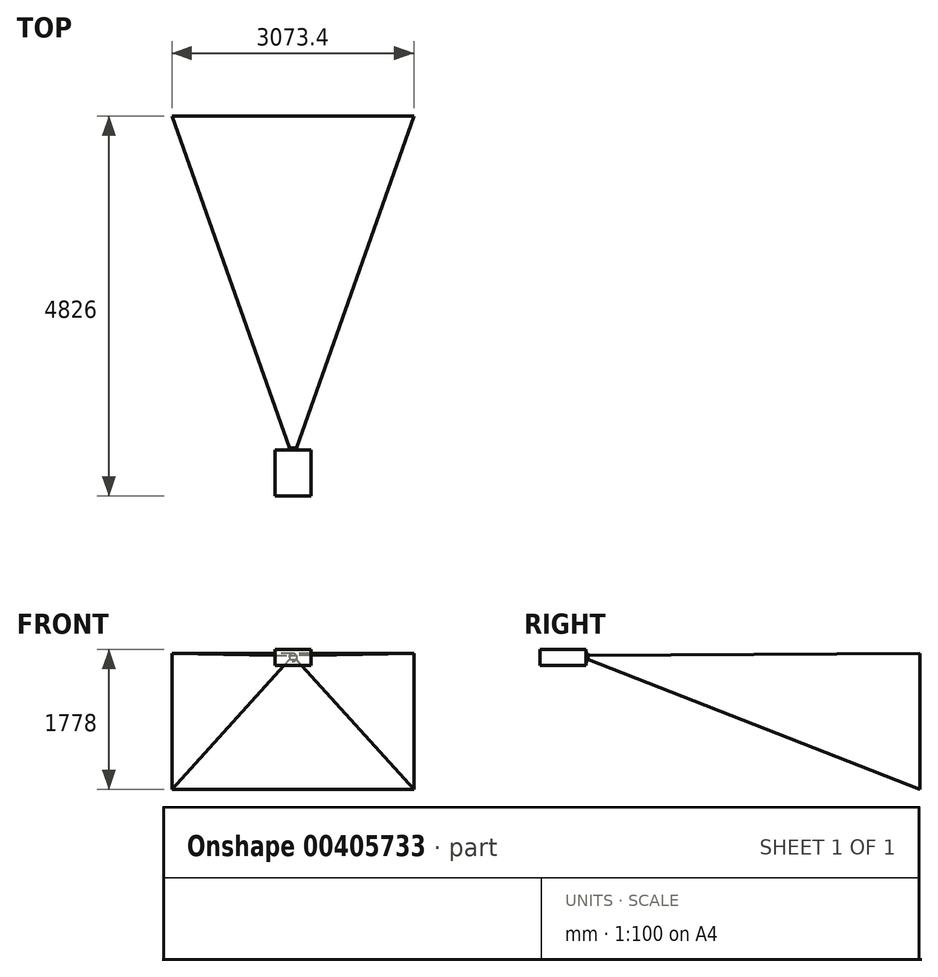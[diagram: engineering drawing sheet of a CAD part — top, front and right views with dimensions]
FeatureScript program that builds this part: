
annotation { "Feature Type Name" : "Feature", "Feature Type Description" : "" }
export const myFeature = defineFeature(function(context is Context, id is Id, definition is map)
    precondition{}
    {
        {
            var Q0;
            Q0=qCreatedBy(makeId("Front.planeOp"),FACE);
            var sketch = newSketch(context, id + "F0", { "sketchPlane" : qUnion([Q0])});
            skLineSegment(sketch, "E0.bottom", {"start": v(1536.7, 863.6) * mm, "end": v(-1536.7, 863.6) * mm});
            skLineSegment(sketch, "E0.top", {"start": v(1536.7, -863.6) * mm, "end": v(-1536.7, -863.6) * mm});
            skLineSegment(sketch, "E0.left", {"start": v(1536.7, 863.6) * mm, "end": v(1536.7, -863.6) * mm});
            skLineSegment(sketch, "E0.right", {"start": v(-1536.7, 863.6) * mm, "end": v(-1536.7, -863.6) * mm});
            skPoint(sketch, "E0.middle", {"position": v(0, 0) * mm});
            skSolve(sketch);
        }
        {
            var Q0;
            Q0=qCreatedBy(makeId("Front.planeOp"),FACE);
            cPlane(context, id + "F1", {"entities" : qUnion([Q0]), "cplaneType" : CPlaneType.OFFSET, "offset" : 4216.4 * mm, "width" : 152.4 * mm, "height" : 152.4 * mm});
        }
        {
            var Q0;
            Q0=qCreatedBy(id+"F1.planeOp",FACE);
            var sketch = newSketch(context, id + "F2", { "sketchPlane" : qUnion([Q0])});
            skCircle(sketch, "E1", {"center": v(0, 812.8) * mm, "radius": 50.8 * mm});
            skLineSegment(sketch, "E2.0", {"start": v(1536.7, 863.6) * mm, "end": v(-1536.7, 863.6) * mm, "construction": true});
            skLineSegment(sketch, "E3.bottom", {"start": v(-228.6, 914.4) * mm, "end": v(228.6, 914.4) * mm});
            skLineSegment(sketch, "E3.top", {"start": v(-228.6, 711.2) * mm, "end": v(228.6, 711.2) * mm});
            skLineSegment(sketch, "E3.left", {"start": v(-228.6, 914.4) * mm, "end": v(-228.6, 711.2) * mm});
            skLineSegment(sketch, "E3.right", {"start": v(228.6, 914.4) * mm, "end": v(228.6, 711.2) * mm});
            skLineSegment(sketch, "E4", {"start": v(-228.6, 914.4) * mm, "end": v(228.6, 711.2) * mm, "construction": true});
            skLineSegment(sketch, "E5.bottom", {"start": v(-44, 838.2) * mm, "end": v(44, 838.2) * mm});
            skLineSegment(sketch, "E5.top", {"start": v(-44, 787.4) * mm, "end": v(44, 787.4) * mm});
            skLineSegment(sketch, "E5.left", {"start": v(-44, 838.2) * mm, "end": v(-44, 787.4) * mm});
            skLineSegment(sketch, "E5.right", {"start": v(44, 838.2) * mm, "end": v(44, 787.4) * mm});
            skSolve(sketch);
        }
        {
            var Q0;
            Q0=makeQuery(id+"F0.imprint","IMPRINT",FACE,{"disambiguationData":[TD([[makeQuery(id+"F0.imprint","IMPRINT",EDGE,{"derivedFrom":sQuery(id+"F0.wireOp",EDGE,"E0.bottom")}),1.0]])]});
            var Q1;
            Q1=makeQuery(id+"F2.imprint","IMPRINT",FACE,{"disambiguationData":[TD([[makeQuery(id+"F2.imprint","IMPRINT",EDGE,{"derivedFrom":sQuery(id+"F2.wireOp",EDGE,"E5.bottom")}),-1.0]])]});
            loft(context, id + "F3", {"sheetProfilesArray" : [{ "sheetProfileEntities" : qUnion([Q0]) }, { "sheetProfileEntities" : qUnion([Q1]) }]});
        }
        {
            var Q0;
            {var subQ0=sQuery(id+"F2.wireOp",EDGE,"E5.bottom");Q0=makeQuery(id+"F2.imprint","IMPRINT",FACE,{"disambiguationData":[TD([[makeQuery(id+"F2.imprint","IMPRINT",EDGE,{"derivedFrom":subQ0}),1.0]])]});}
            var Q1;
            Q1=makeQuery(id+"F2.imprint","IMPRINT",FACE,{"disambiguationData":[TD([[makeQuery(id+"F2.imprint","IMPRINT",EDGE,{"derivedFrom":sQuery(id+"F2.wireOp",EDGE,"E5.bottom")}),-1.0]])]});
            var Q2;
            {var subQ0=sQuery(id+"F2.wireOp",EDGE,"E5.top");Q2=makeQuery(id+"F2.imprint","IMPRINT",FACE,{"disambiguationData":[TD([[makeQuery(id+"F2.imprint","IMPRINT",EDGE,{"derivedFrom":subQ0}),-1.0]])]});}
            var Q3;
            {var subQ0=sQuery(id+"F2.wireOp",EDGE,"E5.left");Q3=makeQuery(id+"F2.imprint","IMPRINT",FACE,{"disambiguationData":[TD([[makeQuery(id+"F2.imprint","IMPRINT",EDGE,{"derivedFrom":subQ0}),-1.0]])]});}
            var Q4;
            {var subQ0=sQuery(id+"F2.wireOp",EDGE,"E5.right");Q4=makeQuery(id+"F2.imprint","IMPRINT",FACE,{"disambiguationData":[TD([[makeQuery(id+"F2.imprint","IMPRINT",EDGE,{"derivedFrom":subQ0}),1.0]])]});}
            extrude(context, id + "F4", {"entities" : qUnion([Q0, Q1, Q2, Q3, Q4]), "depth" : 25.4 * mm, "offsetDistance" : 25.4 * mm});
        }
        {
            var Q0;
            {var subQ0=sQuery(id+"F2.wireOp",EDGE,"E5.right");Q0=makeQuery(id+"F2.imprint","IMPRINT",FACE,{"disambiguationData":[TD([[makeQuery(id+"F2.imprint","IMPRINT",EDGE,{"derivedFrom":subQ0}),1.0]])]});}
            var Q1;
            {var subQ0=sQuery(id+"F2.wireOp",EDGE,"E5.bottom");Q1=makeQuery(id+"F2.imprint","IMPRINT",FACE,{"disambiguationData":[TD([[makeQuery(id+"F2.imprint","IMPRINT",EDGE,{"derivedFrom":subQ0}),1.0]])]});}
            var Q2;
            {var subQ0=sQuery(id+"F2.wireOp",EDGE,"E5.top");Q2=makeQuery(id+"F2.imprint","IMPRINT",FACE,{"disambiguationData":[TD([[makeQuery(id+"F2.imprint","IMPRINT",EDGE,{"derivedFrom":subQ0}),-1.0]])]});}
            var Q3;
            {var subQ0=sQuery(id+"F2.wireOp",EDGE,"E5.left");Q3=makeQuery(id+"F2.imprint","IMPRINT",FACE,{"disambiguationData":[TD([[makeQuery(id+"F2.imprint","IMPRINT",EDGE,{"derivedFrom":subQ0}),-1.0]])]});}
            var Q4;
            Q4=makeQuery(id+"F2.imprint","IMPRINT",FACE,{"disambiguationData":[TD([[makeQuery(id+"F2.imprint","IMPRINT",EDGE,{"derivedFrom":sQuery(id+"F2.wireOp",EDGE,"E5.bottom")}),-1.0]])]});
            var Q5;
            Q5=makeQuery(id+"F2.imprint","IMPRINT",FACE,{"disambiguationData":[TD([[makeQuery(id+"F2.imprint","IMPRINT",EDGE,{"derivedFrom":sQuery(id+"F2.wireOp",EDGE,"E3.bottom")}),-1.0]])]});
            extrude(context, id + "F5", {"entities" : qUnion([Q0, Q1, Q2, Q3, Q4, Q5]), "operationType" : NewBodyOperationType.ADD, "depth" : 609.6 * mm, "offsetDistance" : 25.4 * mm, "hasSecondDirection" : true, "secondDirectionOppositeDirection" : false, "secondDirectionDepth" : 25.4 * mm});
        }
    });
